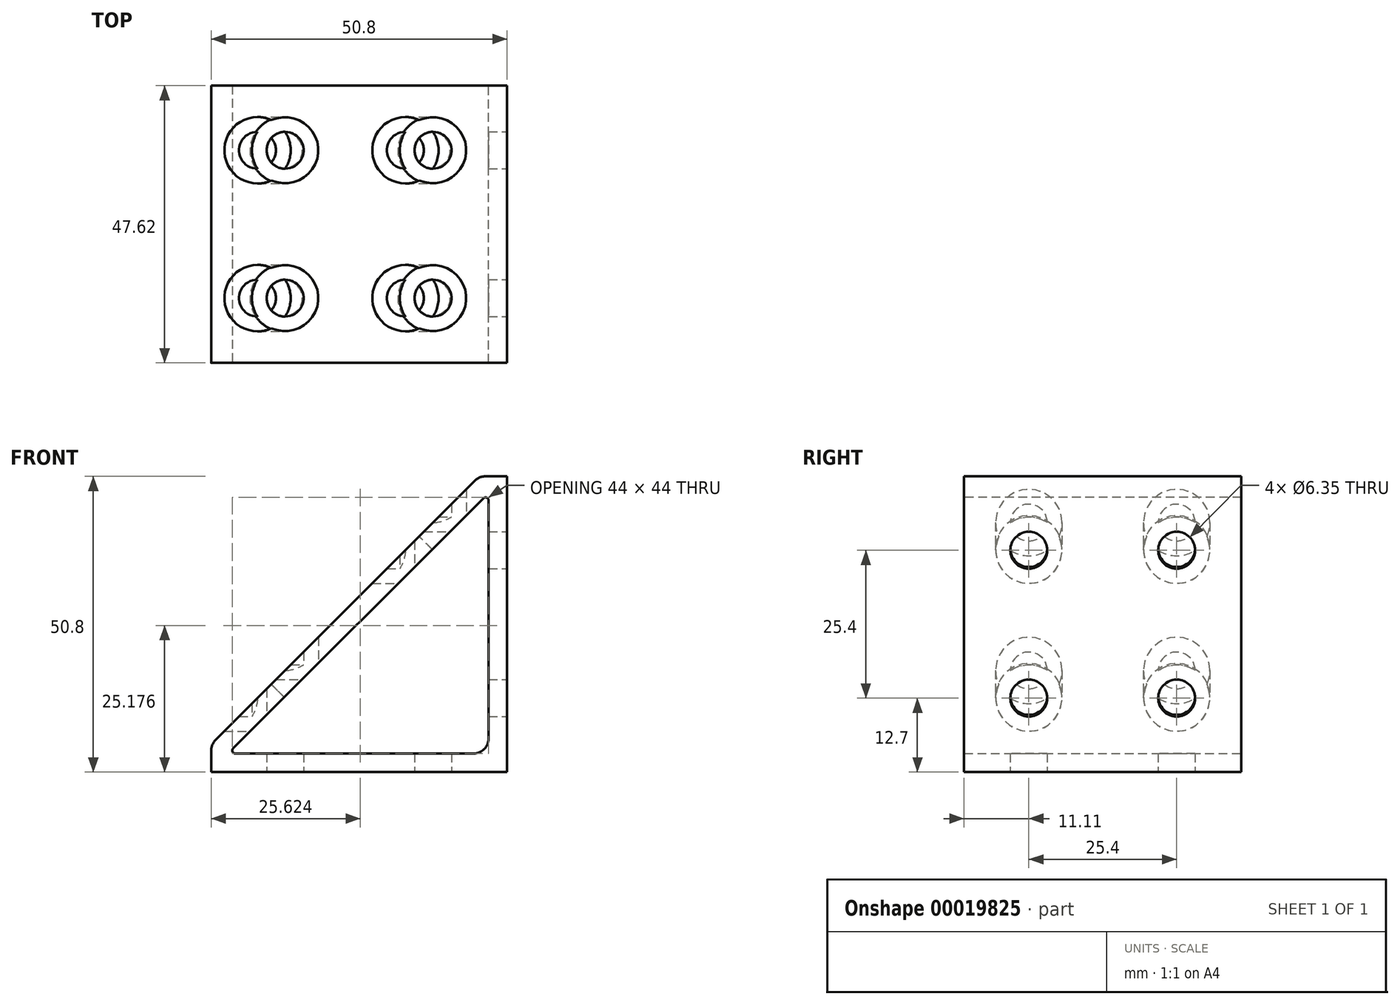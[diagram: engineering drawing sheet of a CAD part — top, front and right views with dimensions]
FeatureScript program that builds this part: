
annotation { "Feature Type Name" : "Feature", "Feature Type Description" : "" }
export const myFeature = defineFeature(function(context is Context, id is Id, definition is map)
    precondition{}
    {
        {
            var Q0;
            Q0=qCreatedBy(makeId("Front.planeOp"),FACE);
            var sketch = newSketch(context, id + "F0", { "sketchPlane" : qUnion([Q0])});
            skLineSegment(sketch, "E0.bottom", {"start": v(0, 0) * mm, "end": v(-50.8, 0) * mm});
            skLineSegment(sketch, "E0.left", {"start": v(0, 0) * mm, "end": v(0, 50.8) * mm});
            skLineSegment(sketch, "E1", {"start": v(-4.76, 50.8) * mm, "end": v(-50.8, 4.76) * mm});
            skLineSegment(sketch, "E2", {"start": v(0, 50.8) * mm, "end": v(-4.76, 50.8) * mm});
            skLineSegment(sketch, "E3", {"start": v(-50.8, 4.76) * mm, "end": v(-50.8, 0) * mm});
            skLineSegment(sketch, "E4", {"start": v(-3.17, 47.9) * mm, "end": v(-47.9, 3.17) * mm});
            skLineSegment(sketch, "E5", {"start": v(-47.9, 3.18) * mm, "end": v(-3.18, 3.18) * mm});
            skLineSegment(sketch, "E6", {"start": v(-3.18, 3.18) * mm, "end": v(-3.18, 47.9) * mm});
            skSolve(sketch);
        }
        {
            var Q0;
            Q0=makeQuery(id+"F0.imprint","IMPRINT",FACE,{"disambiguationData":[TD([[makeQuery(id+"F0.imprint","IMPRINT",EDGE,{"derivedFrom":sQuery(id+"F0.wireOp",EDGE,"E0.bottom")}),-1.0]])]});
            extrude(context, id + "F1", {"entities" : qUnion([Q0]), "endBound" : BoundingType.SYMMETRIC, "depth" : 50.8 * mm});
        }
        {
            var Q0;
            Q0=makeQuery(id+"F1.opExtrude","SWEPT_FACE",FACE,{"disambiguationData":[OSD([sQuery(id+"F0.wireOp",EDGE,"E0.bottom")])]});
            var sketch = newSketch(context, id + "F2", { "sketchPlane" : qUnion([Q0])});
            skLineSegment(sketch, "E7", {"start": v(-12.7, 12.7) * mm, "end": v(-12.7, -12.7) * mm});
            skLineSegment(sketch, "E8.bottom", {"start": v(-12.7, -12.7) * mm, "end": v(-38.1, -12.7) * mm});
            skLineSegment(sketch, "E8.top", {"start": v(-12.7, 12.7) * mm, "end": v(-38.1, 12.7) * mm});
            skLineSegment(sketch, "E8.left", {"start": v(-12.7, -12.7) * mm, "end": v(-12.7, 12.7) * mm});
            skLineSegment(sketch, "E8.right", {"start": v(-38.1, -12.7) * mm, "end": v(-38.1, 12.7) * mm});
            skSolve(sketch);
        }
        {
            var Q0;
            Q0=sQuery(id+"F2.wireOp",VERTEX,"E7.start");
            var Q1;
            Q1=sQuery(id+"F2.wireOp",VERTEX,"E7.end");
            var Q2;
            Q2=sQuery(id+"F2.wireOp",VERTEX,"E8.right.start");
            var Q3;
            Q3=sQuery(id+"F2.wireOp",VERTEX,"E8.right.end");
            var Q4;
            Q4=makeQuery(id+"F1.opExtrude","SWEPT_BODY",BODY,{"disambiguationData":[OSD([sQuery(id+"F0.wireOp",EDGE,"E0.bottom"),sQuery(id+"F0.wireOp",EDGE,"E0.left"),sQuery(id+"F0.wireOp",EDGE,"E1"),sQuery(id+"F0.wireOp",EDGE,"E2"),sQuery(id+"F0.wireOp",EDGE,"E3"),sQuery(id+"F0.wireOp",EDGE,"E4"),sQuery(id+"F0.wireOp",EDGE,"E5"),sQuery(id+"F0.wireOp",EDGE,"E6")])]});
            hole(context, id + "F3", {"style" : HoleStyle.SIMPLE, "holeDiameter" : 6.35 * mm, "endStyle" : HoleEndStyle.BLIND, "holeDepth" : 3.17 * mm, "locations" : qUnion([Q0, Q1, Q2, Q3]), "scope" : qUnion([Q4])});
        }
        {
            var Q0;
            Q0=makeQuery(id+"F1.opExtrude","SWEPT_FACE",FACE,{"disambiguationData":[OSD([sQuery(id+"F0.wireOp",EDGE,"E5")])]});
            var sketch = newSketch(context, id + "F4", { "sketchPlane" : qUnion([Q0])});
            skCircle(sketch, "E9", {"center": v(-12.7, -12.7) * mm, "radius": 5.72 * mm});
            skCircle(sketch, "E10", {"center": v(-12.7, 12.7) * mm, "radius": 5.72 * mm});
            skCircle(sketch, "E11", {"center": v(-38.1, 12.7) * mm, "radius": 5.72 * mm});
            skCircle(sketch, "E12", {"center": v(-38.1, -12.7) * mm, "radius": 5.72 * mm});
            skSolve(sketch);
        }
        {
            var Q0;
            Q0=makeQuery(id+"F4.imprint","IMPRINT",FACE,{"disambiguationData":[TD([[makeQuery(id+"F4.imprint","IMPRINT",EDGE,{"derivedFrom":sQuery(id+"F4.wireOp",EDGE,"E9")}),1.0]])]});
            var Q1;
            Q1=makeQuery(id+"F4.imprint","IMPRINT",FACE,{"disambiguationData":[TD([[makeQuery(id+"F4.imprint","IMPRINT",EDGE,{"derivedFrom":makeQuery(id+"F3.hole-0.boolean.opBoolean","COPY",EDGE,{"derivedFrom":makeQuery(id+"F3.hole-0.opRevolve","SWEPT_EDGE",EDGE,{"disambiguationData":[OSD([sQuery(id+"F3.hole-0.sketch.wireOp",EDGE,"core_line_1"),sQuery(id+"F3.hole-0.sketch.wireOp",EDGE,"core_line_2")])]})})}),-1.0]])]});
            var Q2;
            Q2=makeQuery(id+"F4.imprint","IMPRINT",FACE,{"disambiguationData":[TD([[makeQuery(id+"F4.imprint","IMPRINT",EDGE,{"derivedFrom":makeQuery(id+"F3.hole-1.boolean.opBoolean","COPY",EDGE,{"derivedFrom":makeQuery(id+"F3.hole-1.opRevolve","SWEPT_EDGE",EDGE,{"disambiguationData":[OSD([sQuery(id+"F3.hole-1.sketch.wireOp",EDGE,"core_line_1"),sQuery(id+"F3.hole-1.sketch.wireOp",EDGE,"core_line_2")])]})})}),-1.0]])]});
            var Q3;
            Q3=makeQuery(id+"F4.imprint","IMPRINT",FACE,{"disambiguationData":[TD([[makeQuery(id+"F4.imprint","IMPRINT",EDGE,{"derivedFrom":sQuery(id+"F4.wireOp",EDGE,"E10")}),1.0]])]});
            var Q4;
            Q4=makeQuery(id+"F4.imprint","IMPRINT",FACE,{"disambiguationData":[TD([[makeQuery(id+"F4.imprint","IMPRINT",EDGE,{"derivedFrom":sQuery(id+"F4.wireOp",EDGE,"E11")}),1.0]])]});
            var Q5;
            Q5=makeQuery(id+"F4.imprint","IMPRINT",FACE,{"disambiguationData":[TD([[makeQuery(id+"F4.imprint","IMPRINT",EDGE,{"derivedFrom":makeQuery(id+"F3.hole-2.boolean.opBoolean","COPY",EDGE,{"derivedFrom":makeQuery(id+"F3.hole-2.opRevolve","SWEPT_EDGE",EDGE,{"disambiguationData":[OSD([sQuery(id+"F3.hole-2.sketch.wireOp",EDGE,"core_line_1"),sQuery(id+"F3.hole-2.sketch.wireOp",EDGE,"core_line_2")])]})})}),-1.0]])]});
            var Q6;
            Q6=makeQuery(id+"F4.imprint","IMPRINT",FACE,{"disambiguationData":[TD([[makeQuery(id+"F4.imprint","IMPRINT",EDGE,{"derivedFrom":makeQuery(id+"F3.hole-3.boolean.opBoolean","COPY",EDGE,{"derivedFrom":makeQuery(id+"F3.hole-3.opRevolve","SWEPT_EDGE",EDGE,{"disambiguationData":[OSD([sQuery(id+"F3.hole-3.sketch.wireOp",EDGE,"core_line_1"),sQuery(id+"F3.hole-3.sketch.wireOp",EDGE,"core_line_2")])]})})}),-1.0]])]});
            var Q7;
            Q7=makeQuery(id+"F4.imprint","IMPRINT",FACE,{"disambiguationData":[TD([[makeQuery(id+"F4.imprint","IMPRINT",EDGE,{"derivedFrom":sQuery(id+"F4.wireOp",EDGE,"E12")}),1.0]])]});
            extrude(context, id + "F5", {"entities" : qUnion([Q0, Q1, Q2, Q3, Q4, Q5, Q6, Q7]), "operationType" : NewBodyOperationType.REMOVE, "endBound" : BoundingType.THROUGH_ALL, "depth" : 25.4 * mm});
        }
        {
            var Q0;
            Q0=makeQuery(id+"F1.opExtrude","SWEPT_FACE",FACE,{"disambiguationData":[OSD([sQuery(id+"F0.wireOp",EDGE,"E0.left")])]});
            var sketch = newSketch(context, id + "F6", { "sketchPlane" : qUnion([Q0])});
            skLineSegment(sketch, "E13", {"start": v(-12.7, 12.7) * mm, "end": v(12.7, 12.7) * mm});
            skLineSegment(sketch, "E14.top", {"start": v(-12.7, 38.1) * mm, "end": v(12.7, 38.1) * mm});
            skLineSegment(sketch, "E14.left", {"start": v(-12.7, 12.7) * mm, "end": v(-12.7, 38.1) * mm});
            skLineSegment(sketch, "E14.right", {"start": v(12.7, 12.7) * mm, "end": v(12.7, 38.1) * mm});
            skSolve(sketch);
        }
        {
            var Q0;
            Q0=sQuery(id+"F6.wireOp",VERTEX,"E13.start");
            var Q1;
            Q1=sQuery(id+"F6.wireOp",VERTEX,"E13.end");
            var Q2;
            Q2=sQuery(id+"F6.wireOp",VERTEX,"E14.top.start");
            var Q3;
            Q3=sQuery(id+"F6.wireOp",VERTEX,"E14.right.end");
            var Q4;
            Q4=makeQuery(id+"F1.opExtrude","SWEPT_BODY",BODY,{"disambiguationData":[OSD([sQuery(id+"F0.wireOp",EDGE,"E0.bottom"),sQuery(id+"F0.wireOp",EDGE,"E0.left"),sQuery(id+"F0.wireOp",EDGE,"E1"),sQuery(id+"F0.wireOp",EDGE,"E2"),sQuery(id+"F0.wireOp",EDGE,"E3"),sQuery(id+"F0.wireOp",EDGE,"E4"),sQuery(id+"F0.wireOp",EDGE,"E5"),sQuery(id+"F0.wireOp",EDGE,"E6")])]});
            hole(context, id + "F7", {"style" : HoleStyle.SIMPLE, "holeDiameter" : 6.35 * mm, "endStyle" : HoleEndStyle.BLIND, "holeDepth" : 3.17 * mm, "locations" : qUnion([Q0, Q1, Q2, Q3]), "scope" : qUnion([Q4])});
        }
        {
            var Q0;
            Q0=makeQuery(id+"F1.opExtrude","SWEPT_FACE",FACE,{"disambiguationData":[OSD([sQuery(id+"F0.wireOp",EDGE,"E6")])]});
            var sketch = newSketch(context, id + "F8", { "sketchPlane" : qUnion([Q0])});
            skCircle(sketch, "E15", {"center": v(12.7, 12.7) * mm, "radius": 5.72 * mm});
            skCircle(sketch, "E16", {"center": v(-12.7, 12.7) * mm, "radius": 5.72 * mm});
            skCircle(sketch, "E17", {"center": v(12.7, 38.1) * mm, "radius": 5.72 * mm});
            skCircle(sketch, "E18", {"center": v(-12.7, 38.1) * mm, "radius": 5.72 * mm});
            skSolve(sketch);
        }
        {
            var Q0;
            Q0=makeQuery(id+"F8.imprint","IMPRINT",FACE,{"disambiguationData":[TD([[makeQuery(id+"F8.imprint","IMPRINT",EDGE,{"derivedFrom":sQuery(id+"F8.wireOp",EDGE,"E15")}),1.0]])]});
            var Q1;
            Q1=makeQuery(id+"F8.imprint","IMPRINT",FACE,{"disambiguationData":[TD([[makeQuery(id+"F8.imprint","IMPRINT",EDGE,{"derivedFrom":makeQuery(id+"F7.hole-0.boolean.opBoolean","COPY",EDGE,{"derivedFrom":makeQuery(id+"F7.hole-0.opRevolve","SWEPT_EDGE",EDGE,{"disambiguationData":[OSD([sQuery(id+"F7.hole-0.sketch.wireOp",EDGE,"core_line_1"),sQuery(id+"F7.hole-0.sketch.wireOp",EDGE,"core_line_2")])]})})}),-1.0]])]});
            var Q2;
            Q2=makeQuery(id+"F8.imprint","IMPRINT",FACE,{"disambiguationData":[TD([[makeQuery(id+"F8.imprint","IMPRINT",EDGE,{"derivedFrom":sQuery(id+"F8.wireOp",EDGE,"E16")}),1.0]])]});
            var Q3;
            Q3=makeQuery(id+"F8.imprint","IMPRINT",FACE,{"disambiguationData":[TD([[makeQuery(id+"F8.imprint","IMPRINT",EDGE,{"derivedFrom":makeQuery(id+"F7.hole-1.boolean.opBoolean","COPY",EDGE,{"derivedFrom":makeQuery(id+"F7.hole-1.opRevolve","SWEPT_EDGE",EDGE,{"disambiguationData":[OSD([sQuery(id+"F7.hole-1.sketch.wireOp",EDGE,"core_line_1"),sQuery(id+"F7.hole-1.sketch.wireOp",EDGE,"core_line_2")])]})})}),-1.0]])]});
            var Q4;
            Q4=makeQuery(id+"F8.imprint","IMPRINT",FACE,{"disambiguationData":[TD([[makeQuery(id+"F8.imprint","IMPRINT",EDGE,{"derivedFrom":sQuery(id+"F8.wireOp",EDGE,"E17")}),1.0]])]});
            var Q5;
            Q5=makeQuery(id+"F8.imprint","IMPRINT",FACE,{"disambiguationData":[TD([[makeQuery(id+"F8.imprint","IMPRINT",EDGE,{"derivedFrom":makeQuery(id+"F7.hole-2.boolean.opBoolean","COPY",EDGE,{"derivedFrom":makeQuery(id+"F7.hole-2.opRevolve","SWEPT_EDGE",EDGE,{"disambiguationData":[OSD([sQuery(id+"F7.hole-2.sketch.wireOp",EDGE,"core_line_1"),sQuery(id+"F7.hole-2.sketch.wireOp",EDGE,"core_line_2")])]})})}),-1.0]])]});
            var Q6;
            Q6=makeQuery(id+"F8.imprint","IMPRINT",FACE,{"disambiguationData":[TD([[makeQuery(id+"F8.imprint","IMPRINT",EDGE,{"derivedFrom":sQuery(id+"F8.wireOp",EDGE,"E18")}),1.0]])]});
            var Q7;
            Q7=makeQuery(id+"F8.imprint","IMPRINT",FACE,{"disambiguationData":[TD([[makeQuery(id+"F8.imprint","IMPRINT",EDGE,{"derivedFrom":makeQuery(id+"F7.hole-3.boolean.opBoolean","COPY",EDGE,{"derivedFrom":makeQuery(id+"F7.hole-3.opRevolve","SWEPT_EDGE",EDGE,{"disambiguationData":[OSD([sQuery(id+"F7.hole-3.sketch.wireOp",EDGE,"core_line_1"),sQuery(id+"F7.hole-3.sketch.wireOp",EDGE,"core_line_2")])]})})}),-1.0]])]});
            extrude(context, id + "F9", {"entities" : qUnion([Q0, Q1, Q2, Q3, Q4, Q5, Q6, Q7]), "operationType" : NewBodyOperationType.REMOVE, "depth" : 50.8 * mm});
        }
        {
            var Q0;
            Q0=makeQuery(id+"F1.opExtrude","SWEPT_EDGE",EDGE,{"disambiguationData":[OSD([sQuery(id+"F0.wireOp",EDGE,"E1"),sQuery(id+"F0.wireOp",EDGE,"E2")])]});
            var Q1;
            Q1=makeQuery(id+"F1.opExtrude","SWEPT_EDGE",EDGE,{"disambiguationData":[OSD([sQuery(id+"F0.wireOp",EDGE,"E1"),sQuery(id+"F0.wireOp",EDGE,"E3")])]});
            var Q2;
            Q2=makeQuery(id+"F1.opExtrude","SWEPT_EDGE",EDGE,{"disambiguationData":[OSD([sQuery(id+"F0.wireOp",EDGE,"E5"),sQuery(id+"F0.wireOp",EDGE,"E6")])]});
            fillet(context, id + "F10", {"entities" : qUnion([Q0, Q1, Q2]), "radius" : 2.54 * mm, "tangentPropagation" : true, "allowEdgeOverflow" : false});
        }
        {
            var Q0;
            Q0=makeQuery(id+"F1.opExtrude","SWEPT_EDGE",EDGE,{"disambiguationData":[OSD([sQuery(id+"F0.wireOp",EDGE,"E4"),sQuery(id+"F0.wireOp",EDGE,"E6")])]});
            var Q1;
            Q1=makeQuery(id+"F1.opExtrude","SWEPT_EDGE",EDGE,{"disambiguationData":[OSD([sQuery(id+"F0.wireOp",EDGE,"E4"),sQuery(id+"F0.wireOp",EDGE,"E5")])]});
            fillet(context, id + "F11", {"entities" : qUnion([Q0, Q1]), "radius" : 0.5 * mm, "tangentPropagation" : true, "allowEdgeOverflow" : false});
        }
        {
            var Q0;
            Q0=makeQuery(id+"F1.opExtrude","CAP_FACE",FACE,{"disambiguationData":[OSD([sQuery(id+"F0.wireOp",EDGE,"E0.bottom"),sQuery(id+"F0.wireOp",EDGE,"E0.left"),sQuery(id+"F0.wireOp",EDGE,"E1"),sQuery(id+"F0.wireOp",EDGE,"E2"),sQuery(id+"F0.wireOp",EDGE,"E3"),sQuery(id+"F0.wireOp",EDGE,"E4"),sQuery(id+"F0.wireOp",EDGE,"E5"),sQuery(id+"F0.wireOp",EDGE,"E6")])],"isStart":false});
            extrude(context, id + "F12", {"entities" : qUnion([Q0]), "operationType" : NewBodyOperationType.REMOVE, "oppositeDirection" : true, "depth" : 1.59 * mm});
        }
        {
            var Q0;
            Q0=makeQuery(id+"F1.opExtrude","CAP_FACE",FACE,{"disambiguationData":[OSD([sQuery(id+"F0.wireOp",EDGE,"E0.bottom"),sQuery(id+"F0.wireOp",EDGE,"E0.left"),sQuery(id+"F0.wireOp",EDGE,"E1"),sQuery(id+"F0.wireOp",EDGE,"E2"),sQuery(id+"F0.wireOp",EDGE,"E3"),sQuery(id+"F0.wireOp",EDGE,"E4"),sQuery(id+"F0.wireOp",EDGE,"E5"),sQuery(id+"F0.wireOp",EDGE,"E6")])],"isStart":true});
            extrude(context, id + "F13", {"entities" : qUnion([Q0]), "operationType" : NewBodyOperationType.REMOVE, "oppositeDirection" : true, "depth" : 1.59 * mm});
        }
    });
